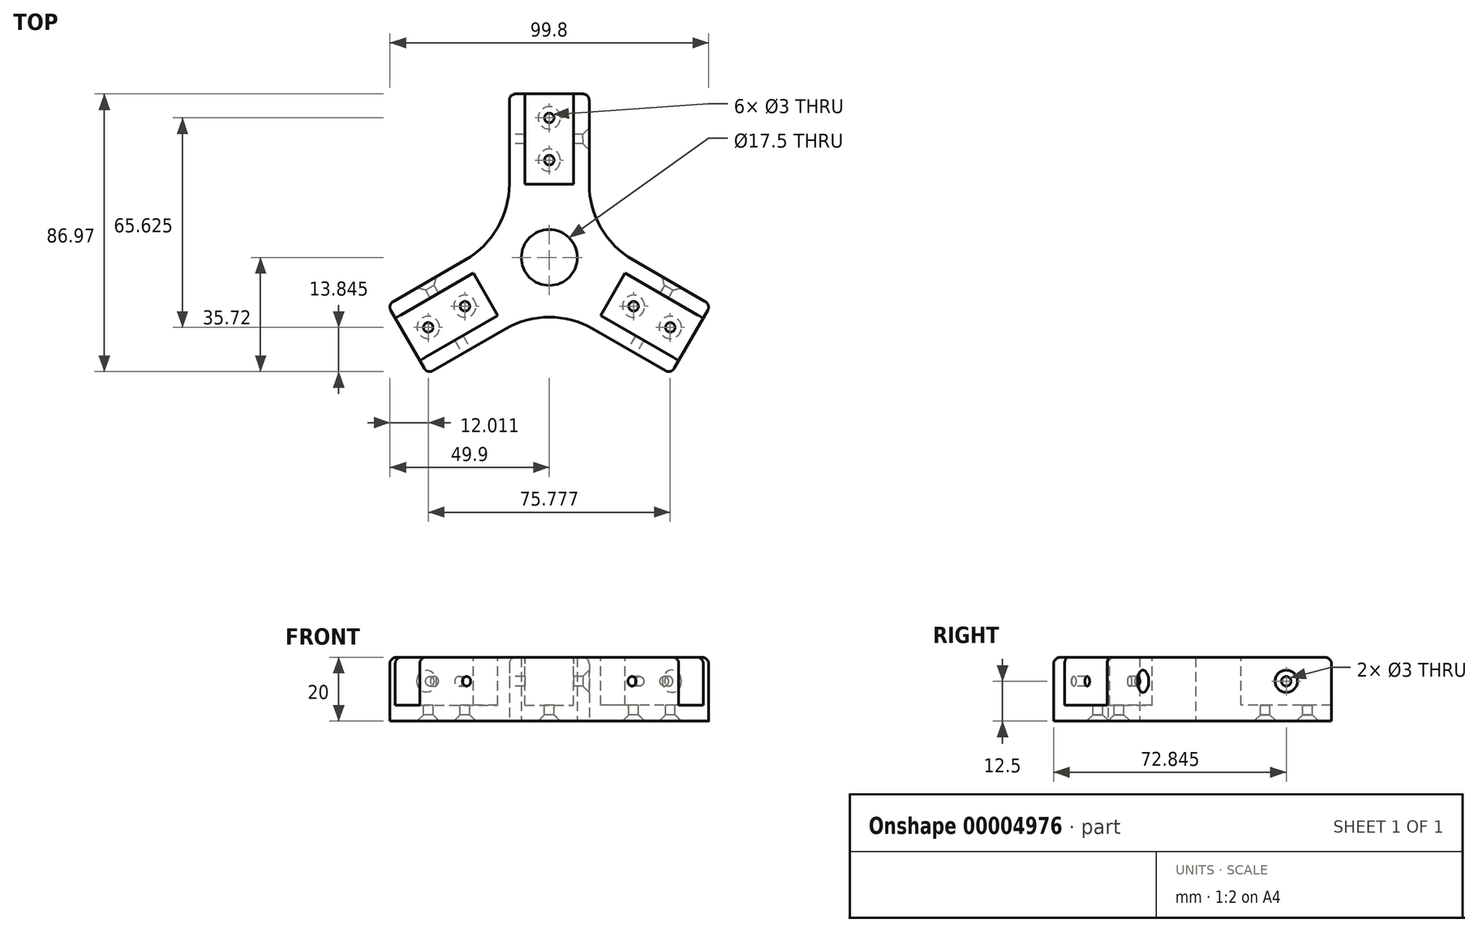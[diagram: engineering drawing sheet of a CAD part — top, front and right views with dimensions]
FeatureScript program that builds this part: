
annotation { "Feature Type Name" : "Feature", "Feature Type Description" : "" }
export const myFeature = defineFeature(function(context is Context, id is Id, definition is map)
    precondition{}
    {
        {
            var Q0;
            Q0=qCreatedBy(makeId("Top.planeOp"),FACE);
            var sketch = newSketch(context, id + "F0", { "sketchPlane" : qUnion([Q0])});
            skCircle(sketch, "E0", {"center": v(0, 0) * mm, "radius": 6.25 * mm, "construction": true});
            skLineSegment(sketch, "E1", {"start": v(0, 0) * mm, "end": v(0, 51.25) * mm, "construction": true});
            skLineSegment(sketch, "E2", {"start": v(-12.5, 51.25) * mm, "end": v(12.5, 51.25) * mm});
            skLineSegment(sketch, "E3", {"start": v(0, 0) * mm, "end": v(44.38, -25.62) * mm, "construction": true});
            skLineSegment(sketch, "E4", {"start": v(12.5, 51.25) * mm, "end": v(12.5, 23) * mm});
            skLineSegment(sketch, "E5", {"start": v(38.13, -36.45) * mm, "end": v(50.63, -14.8) * mm});
            skLineSegment(sketch, "E6", {"start": v(50.63, -14.8) * mm, "end": v(26.17, -0.67) * mm});
            skArc(sketch, "E7", {"start": v(12.5, 23) * mm, "mid": v(16.16, 9.33) * mm, "end": v(26.17, -0.67) * mm});
            skPoint(sketch, "E8", {"position": v(0, 6.25) * mm});
            skLineSegment(sketch, "E9.1.0", {"start": v(-50.63, -14.8) * mm, "end": v(-26.17, -0.67) * mm});
            skArc(sketch, "E9.1.1", {"start": v(-26.17, -0.67) * mm, "mid": v(-16.16, 9.33) * mm, "end": v(-12.5, 23) * mm});
            skLineSegment(sketch, "E9.1.2", {"start": v(-12.5, 51.25) * mm, "end": v(-12.5, 23) * mm});
            skLineSegment(sketch, "E9.2.0", {"start": v(38.13, -36.45) * mm, "end": v(13.67, -22.33) * mm});
            skArc(sketch, "E9.2.1", {"start": v(13.67, -22.33) * mm, "mid": v(0, -18.66) * mm, "end": v(-13.67, -22.33) * mm});
            skLineSegment(sketch, "E9.2.2", {"start": v(-38.13, -36.45) * mm, "end": v(-13.67, -22.33) * mm});
            skLineSegment(sketch, "E10", {"start": v(-50.63, -14.8) * mm, "end": v(-38.13, -36.45) * mm});
            skLineSegment(sketch, "E11", {"start": v(-12.5, 23) * mm, "end": v(12.5, 23) * mm, "construction": true});
            skCircle(sketch, "E12", {"center": v(0, 0) * mm, "radius": 8.75 * mm});
            skSolve(sketch);
        }
        {
            var Q0;
            Q0 = qSketchRegion(id + "F0", true);
            extrude(context, id + "F1", {"entities" : qUnion([Q0]), "depth" : 20 * mm});
        }
        {
            var Q0;
            Q0=makeQuery(id+"F1.opExtrude","CAP_FACE",FACE,{"disambiguationData":[OSD([sQuery(id+"F0.wireOp",EDGE,"E0"),sQuery(id+"F0.wireOp",EDGE,"E2"),sQuery(id+"F0.wireOp",EDGE,"E4"),sQuery(id+"F0.wireOp",EDGE,"E5"),sQuery(id+"F0.wireOp",EDGE,"E6"),sQuery(id+"F0.wireOp",EDGE,"E7"),sQuery(id+"F0.wireOp",EDGE,"E9.1.0"),sQuery(id+"F0.wireOp",EDGE,"E9.1.1"),sQuery(id+"F0.wireOp",EDGE,"E9.1.2"),sQuery(id+"F0.wireOp",EDGE,"E9.2.0"),sQuery(id+"F0.wireOp",EDGE,"E9.2.1"),sQuery(id+"F0.wireOp",EDGE,"E9.2.2"),sQuery(id+"F0.wireOp",EDGE,"E10")])],"isStart":false});
            var sketch = newSketch(context, id + "F2", { "sketchPlane" : qUnion([Q0])});
            skLineSegment(sketch, "E13", {"start": v(0, 0) * mm, "end": v(0, 51.25) * mm, "construction": true});
            skLineSegment(sketch, "E14", {"start": v(-12.5, 23) * mm, "end": v(12.5, 23) * mm, "construction": true});
            skLineSegment(sketch, "E15.bottom", {"start": v(-7.68, 51.25) * mm, "end": v(7.67, 51.25) * mm});
            skLineSegment(sketch, "E15.top", {"start": v(-7.68, 23) * mm, "end": v(7.67, 23) * mm});
            skLineSegment(sketch, "E15.left", {"start": v(-7.68, 51.25) * mm, "end": v(-7.68, 23) * mm});
            skLineSegment(sketch, "E15.right", {"start": v(7.67, 51.25) * mm, "end": v(7.67, 23) * mm});
            skLineSegment(sketch, "E16.1.0", {"start": v(-48.22, -18.98) * mm, "end": v(-23.76, -4.85) * mm});
            skLineSegment(sketch, "E16.1.1", {"start": v(-40.55, -32.27) * mm, "end": v(-48.22, -18.98) * mm});
            skLineSegment(sketch, "E16.1.2", {"start": v(-40.55, -32.27) * mm, "end": v(-16.08, -18.15) * mm});
            skLineSegment(sketch, "E16.1.3", {"start": v(-16.08, -18.15) * mm, "end": v(-23.76, -4.85) * mm});
            skLineSegment(sketch, "E16.2.0", {"start": v(40.55, -32.27) * mm, "end": v(16.08, -18.15) * mm});
            skLineSegment(sketch, "E16.2.1", {"start": v(48.22, -18.98) * mm, "end": v(40.55, -32.27) * mm});
            skLineSegment(sketch, "E16.2.2", {"start": v(48.22, -18.98) * mm, "end": v(23.76, -4.85) * mm});
            skLineSegment(sketch, "E16.2.3", {"start": v(23.76, -4.85) * mm, "end": v(16.08, -18.15) * mm});
            skPoint(sketch, "E16.center", {"position": v(0, 0) * mm});
            skSolve(sketch);
        }
        {
            var Q0;
            Q0 = qSketchRegion(id + "F2", true);
            extrude(context, id + "F3", {"entities" : qUnion([Q0]), "operationType" : NewBodyOperationType.REMOVE, "oppositeDirection" : true, "depth" : 15 * mm});
        }
        {
            var Q0;
            Q0=makeQuery(id+"F3.boolean.opBoolean","COPY",FACE,{"derivedFrom":makeQuery(id+"F3.opExtrude","CAP_FACE",FACE,{"disambiguationData":[OSD([sQuery(id+"F2.wireOp",EDGE,"E15.bottom"),sQuery(id+"F2.wireOp",EDGE,"E15.top"),sQuery(id+"F2.wireOp",EDGE,"E15.left"),sQuery(id+"F2.wireOp",EDGE,"E15.right")])],"isStart":false})});
            var sketch = newSketch(context, id + "F4", { "sketchPlane" : qUnion([Q0])});
            skLineSegment(sketch, "E17", {"start": v(0, 51.25) * mm, "end": v(0, 23) * mm, "construction": true});
            skCircle(sketch, "E18", {"center": v(0, 43.75) * mm, "radius": 1.5 * mm});
            skCircle(sketch, "E19", {"center": v(0, 30.5) * mm, "radius": 1.5 * mm});
            skCircle(sketch, "E20.1.0", {"center": v(-37.89, -21.87) * mm, "radius": 1.5 * mm});
            skCircle(sketch, "E20.1.1", {"center": v(-26.41, -15.25) * mm, "radius": 1.5 * mm});
            skCircle(sketch, "E20.2.0", {"center": v(37.89, -21.87) * mm, "radius": 1.5 * mm});
            skCircle(sketch, "E20.2.1", {"center": v(26.41, -15.25) * mm, "radius": 1.5 * mm});
            skPoint(sketch, "E20.center", {"position": v(0, 0) * mm});
            skSolve(sketch);
        }
        {
            var Q0;
            Q0 = qSketchRegion(id + "F4", true);
            extrude(context, id + "F5", {"entities" : qUnion([Q0]), "operationType" : NewBodyOperationType.REMOVE, "endBound" : BoundingType.THROUGH_ALL, "oppositeDirection" : true, "depth" : 25 * mm});
        }
        {
            var Q0;
            {var subQ0=sQuery(id+"F0.wireOp",EDGE,"E2");var subQ1=sQuery(id+"F0.wireOp",EDGE,"E9.1.2");Q0=makeQuery(id+"F3.boolean.opBoolean","SPLIT",EDGE,{"disambiguationData":[TD([makeQuery(id+"F1.opExtrude","SWEPT_FACE",FACE,{"disambiguationData":[OSD([subQ1])]})])],"derivedFrom":makeQuery(id+"F1.opExtrude","CAP_EDGE",EDGE,{"disambiguationData":[OSD([subQ0])],"isStart":false})});}
            var Q1;
            {var subQ0=sQuery(id+"F0.wireOp",EDGE,"E2");var subQ1=sQuery(id+"F0.wireOp",EDGE,"E4");Q1=makeQuery(id+"F3.boolean.opBoolean","SPLIT",EDGE,{"disambiguationData":[TD([makeQuery(id+"F1.opExtrude","SWEPT_FACE",FACE,{"disambiguationData":[OSD([subQ1])]})])],"derivedFrom":makeQuery(id+"F1.opExtrude","CAP_EDGE",EDGE,{"disambiguationData":[OSD([subQ0])],"isStart":false})});}
            var Q2;
            {var subQ0=sQuery(id+"F0.wireOp",EDGE,"E5");var subQ1=sQuery(id+"F0.wireOp",EDGE,"E6");Q2=makeQuery(id+"F3.boolean.opBoolean","SPLIT",EDGE,{"disambiguationData":[TD([makeQuery(id+"F1.opExtrude","SWEPT_FACE",FACE,{"disambiguationData":[OSD([subQ1])]})])],"derivedFrom":makeQuery(id+"F1.opExtrude","CAP_EDGE",EDGE,{"disambiguationData":[OSD([subQ0])],"isStart":false})});}
            var Q3;
            {var subQ0=sQuery(id+"F0.wireOp",EDGE,"E5");var subQ1=sQuery(id+"F0.wireOp",EDGE,"E9.2.0");Q3=makeQuery(id+"F3.boolean.opBoolean","SPLIT",EDGE,{"disambiguationData":[TD([makeQuery(id+"F1.opExtrude","SWEPT_FACE",FACE,{"disambiguationData":[OSD([subQ1])]})])],"derivedFrom":makeQuery(id+"F1.opExtrude","CAP_EDGE",EDGE,{"disambiguationData":[OSD([subQ0])],"isStart":false})});}
            var Q4;
            {var subQ0=sQuery(id+"F0.wireOp",EDGE,"E10");var subQ1=sQuery(id+"F0.wireOp",EDGE,"E9.2.2");Q4=makeQuery(id+"F3.boolean.opBoolean","SPLIT",EDGE,{"disambiguationData":[TD([makeQuery(id+"F1.opExtrude","SWEPT_FACE",FACE,{"disambiguationData":[OSD([subQ1])]})])],"derivedFrom":makeQuery(id+"F1.opExtrude","CAP_EDGE",EDGE,{"disambiguationData":[OSD([subQ0])],"isStart":false})});}
            var Q5;
            {var subQ0=sQuery(id+"F0.wireOp",EDGE,"E10");var subQ1=sQuery(id+"F0.wireOp",EDGE,"E9.1.0");Q5=makeQuery(id+"F3.boolean.opBoolean","SPLIT",EDGE,{"disambiguationData":[TD([makeQuery(id+"F1.opExtrude","SWEPT_FACE",FACE,{"disambiguationData":[OSD([subQ1])]})])],"derivedFrom":makeQuery(id+"F1.opExtrude","CAP_EDGE",EDGE,{"disambiguationData":[OSD([subQ0])],"isStart":false})});}
            fillet(context, id + "F6", {"entities" : qUnion([Q0, Q1, Q2, Q3, Q4, Q5]), "radius" : 2 * mm, "tangentPropagation" : true, "allowEdgeOverflow" : false});
        }
        {
            var Q0;
            Q0=makeQuery(id+"F1.opExtrude","SWEPT_FACE",FACE,{"disambiguationData":[OSD([sQuery(id+"F0.wireOp",EDGE,"E9.2.2")])]});
            var sketch = newSketch(context, id + "F7", { "sketchPlane" : qUnion([Q0])});
            skLineSegment(sketch, "E21.0", {"start": v(-23, 5) * mm, "end": v(-23, 20) * mm, "construction": true});
            skLineSegment(sketch, "E22", {"start": v(-23, 12.5) * mm, "end": v(-51.25, 12.5) * mm, "construction": true});
            skCircle(sketch, "E23", {"center": v(-37.12, 12.5) * mm, "radius": 1.5 * mm});
            skSolve(sketch);
        }
        {
            var Q0;
            Q0 = qSketchRegion(id + "F7", true);
            extrude(context, id + "F8", {"entities" : qUnion([Q0]), "operationType" : NewBodyOperationType.REMOVE, "endBound" : BoundingType.THROUGH_ALL, "oppositeDirection" : true, "depth" : 25 * mm});
        }
        {
            var Q0;
            Q0=makeQuery(id+"F1.opExtrude","SWEPT_FACE",FACE,{"disambiguationData":[OSD([sQuery(id+"F0.wireOp",EDGE,"E9.2.0")])]});
            var sketch = newSketch(context, id + "F9", { "sketchPlane" : qUnion([Q0])});
            skLineSegment(sketch, "E24.0", {"start": v(23, 5) * mm, "end": v(23, 20) * mm, "construction": true});
            skLineSegment(sketch, "E25", {"start": v(23, 12.5) * mm, "end": v(51.25, 12.5) * mm, "construction": true});
            skCircle(sketch, "E26", {"center": v(37.12, 12.5) * mm, "radius": 1.5 * mm});
            skSolve(sketch);
        }
        {
            var Q0;
            Q0 = qSketchRegion(id + "F9", true);
            extrude(context, id + "F10", {"entities" : qUnion([Q0]), "operationType" : NewBodyOperationType.REMOVE, "endBound" : BoundingType.THROUGH_ALL, "oppositeDirection" : true, "depth" : 25 * mm});
        }
        {
            var Q0;
            Q0=makeQuery(id+"F1.opExtrude","SWEPT_FACE",FACE,{"disambiguationData":[OSD([sQuery(id+"F0.wireOp",EDGE,"E9.1.2")])]});
            var sketch = newSketch(context, id + "F11", { "sketchPlane" : qUnion([Q0])});
            skLineSegment(sketch, "E27.0", {"start": v(-23, 5) * mm, "end": v(-23, 20) * mm, "construction": true});
            skLineSegment(sketch, "E28", {"start": v(-23, 12.5) * mm, "end": v(-51.25, 12.5) * mm, "construction": true});
            skCircle(sketch, "E29", {"center": v(-37.13, 12.5) * mm, "radius": 1.5 * mm});
            skSolve(sketch);
        }
        {
            var Q0;
            Q0 = qSketchRegion(id + "F11", true);
            extrude(context, id + "F12", {"entities" : qUnion([Q0]), "operationType" : NewBodyOperationType.REMOVE, "endBound" : BoundingType.THROUGH_ALL, "oppositeDirection" : true, "depth" : 25 * mm});
        }
        {
            var Q0;
            Q0=makeQuery(id+"F1.opExtrude","SWEPT_EDGE",EDGE,{"disambiguationData":[OSD([sQuery(id+"F0.wireOp",EDGE,"E5"),sQuery(id+"F0.wireOp",EDGE,"E9.2.0")])]});
            var Q1;
            Q1=makeQuery(id+"F1.opExtrude","SWEPT_EDGE",EDGE,{"disambiguationData":[OSD([sQuery(id+"F0.wireOp",EDGE,"E5"),sQuery(id+"F0.wireOp",EDGE,"E6")])]});
            var Q2;
            Q2=makeQuery(id+"F1.opExtrude","SWEPT_EDGE",EDGE,{"disambiguationData":[OSD([sQuery(id+"F0.wireOp",EDGE,"E9.1.0"),sQuery(id+"F0.wireOp",EDGE,"E10")])]});
            fillet(context, id + "F13", {"entities" : qUnion([Q0, Q1, Q2]), "radius" : 2 * mm, "tangentPropagation" : true, "defaultsChanged" : true, "vertexSettings" : [], "allowEdgeOverflow" : false});
        }
        {
            var Q0;
            Q0=makeQuery(id+"F8.boolean.opBoolean","COPY",EDGE,{"derivedFrom":makeQuery(id+"F8.opExtrude","CAP_EDGE",EDGE,{"disambiguationData":[OSD([sQuery(id+"F7.wireOp",EDGE,"E23")])],"isStart":true})});
            var Q1;
            Q1=makeQuery(id+"F10.boolean.opBoolean","COPY",EDGE,{"derivedFrom":makeQuery(id+"F10.opExtrude","CAP_EDGE",EDGE,{"disambiguationData":[OSD([sQuery(id+"F9.wireOp",EDGE,"E26")])],"isStart":true})});
            var Q2;
            Q2=makeQuery(id+"F10.boolean.opBoolean","INTERSECT",EDGE,{"derivedFrom":[makeQuery(id+"F1.opExtrude","SWEPT_FACE",FACE,{"disambiguationData":[OSD([sQuery(id+"F0.wireOp",EDGE,"E6")])]}),makeQuery(id+"F10.opExtrude","SWEPT_FACE",FACE,{"disambiguationData":[OSD([sQuery(id+"F9.wireOp",EDGE,"E26")])]})]});
            var Q3;
            Q3=makeQuery(id+"F12.boolean.opBoolean","INTERSECT",EDGE,{"derivedFrom":[makeQuery(id+"F1.opExtrude","SWEPT_FACE",FACE,{"disambiguationData":[OSD([sQuery(id+"F0.wireOp",EDGE,"E4")])]}),makeQuery(id+"F12.opExtrude","SWEPT_FACE",FACE,{"disambiguationData":[OSD([sQuery(id+"F11.wireOp",EDGE,"E29")])]})]});
            var Q4;
            Q4=makeQuery(id+"F12.boolean.opBoolean","COPY",EDGE,{"derivedFrom":makeQuery(id+"F12.opExtrude","CAP_EDGE",EDGE,{"disambiguationData":[OSD([sQuery(id+"F11.wireOp",EDGE,"E29")])],"isStart":true})});
            var Q5;
            Q5=makeQuery(id+"F8.boolean.opBoolean","INTERSECT",EDGE,{"derivedFrom":[makeQuery(id+"F1.opExtrude","SWEPT_FACE",FACE,{"disambiguationData":[OSD([sQuery(id+"F0.wireOp",EDGE,"E9.1.0")])]}),makeQuery(id+"F8.opExtrude","SWEPT_FACE",FACE,{"disambiguationData":[OSD([sQuery(id+"F7.wireOp",EDGE,"E23")])]})]});
            var Q6;
            Q6=makeQuery(id+"F5.boolean.opBoolean","INTERSECT",EDGE,{"derivedFrom":[makeQuery(id+"F1.opExtrude","CAP_FACE",FACE,{"disambiguationData":[OSD([sQuery(id+"F0.wireOp",EDGE,"E2"),sQuery(id+"F0.wireOp",EDGE,"E4"),sQuery(id+"F0.wireOp",EDGE,"E5"),sQuery(id+"F0.wireOp",EDGE,"E6"),sQuery(id+"F0.wireOp",EDGE,"E7"),sQuery(id+"F0.wireOp",EDGE,"E9.1.0"),sQuery(id+"F0.wireOp",EDGE,"E9.1.1"),sQuery(id+"F0.wireOp",EDGE,"E9.1.2"),sQuery(id+"F0.wireOp",EDGE,"E9.2.0"),sQuery(id+"F0.wireOp",EDGE,"E9.2.1"),sQuery(id+"F0.wireOp",EDGE,"E9.2.2"),sQuery(id+"F0.wireOp",EDGE,"E10"),sQuery(id+"F0.wireOp",EDGE,"E12")])],"isStart":true}),makeQuery(id+"F5.opExtrude","SWEPT_FACE",FACE,{"disambiguationData":[OSD([sQuery(id+"F4.wireOp",EDGE,"E18")])]})]});
            var Q7;
            Q7=makeQuery(id+"F5.boolean.opBoolean","INTERSECT",EDGE,{"derivedFrom":[makeQuery(id+"F1.opExtrude","CAP_FACE",FACE,{"disambiguationData":[OSD([sQuery(id+"F0.wireOp",EDGE,"E2"),sQuery(id+"F0.wireOp",EDGE,"E4"),sQuery(id+"F0.wireOp",EDGE,"E5"),sQuery(id+"F0.wireOp",EDGE,"E6"),sQuery(id+"F0.wireOp",EDGE,"E7"),sQuery(id+"F0.wireOp",EDGE,"E9.1.0"),sQuery(id+"F0.wireOp",EDGE,"E9.1.1"),sQuery(id+"F0.wireOp",EDGE,"E9.1.2"),sQuery(id+"F0.wireOp",EDGE,"E9.2.0"),sQuery(id+"F0.wireOp",EDGE,"E9.2.1"),sQuery(id+"F0.wireOp",EDGE,"E9.2.2"),sQuery(id+"F0.wireOp",EDGE,"E10"),sQuery(id+"F0.wireOp",EDGE,"E12")])],"isStart":true}),makeQuery(id+"F5.opExtrude","SWEPT_FACE",FACE,{"disambiguationData":[OSD([sQuery(id+"F4.wireOp",EDGE,"E19")])]})]});
            var Q8;
            Q8=makeQuery(id+"F5.boolean.opBoolean","INTERSECT",EDGE,{"derivedFrom":[makeQuery(id+"F1.opExtrude","CAP_FACE",FACE,{"disambiguationData":[OSD([sQuery(id+"F0.wireOp",EDGE,"E2"),sQuery(id+"F0.wireOp",EDGE,"E4"),sQuery(id+"F0.wireOp",EDGE,"E5"),sQuery(id+"F0.wireOp",EDGE,"E6"),sQuery(id+"F0.wireOp",EDGE,"E7"),sQuery(id+"F0.wireOp",EDGE,"E9.1.0"),sQuery(id+"F0.wireOp",EDGE,"E9.1.1"),sQuery(id+"F0.wireOp",EDGE,"E9.1.2"),sQuery(id+"F0.wireOp",EDGE,"E9.2.0"),sQuery(id+"F0.wireOp",EDGE,"E9.2.1"),sQuery(id+"F0.wireOp",EDGE,"E9.2.2"),sQuery(id+"F0.wireOp",EDGE,"E10"),sQuery(id+"F0.wireOp",EDGE,"E12")])],"isStart":true}),makeQuery(id+"F5.opExtrude","SWEPT_FACE",FACE,{"disambiguationData":[OSD([sQuery(id+"F4.wireOp",EDGE,"E20.1.1")])]})]});
            var Q9;
            Q9=makeQuery(id+"F5.boolean.opBoolean","INTERSECT",EDGE,{"derivedFrom":[makeQuery(id+"F1.opExtrude","CAP_FACE",FACE,{"disambiguationData":[OSD([sQuery(id+"F0.wireOp",EDGE,"E2"),sQuery(id+"F0.wireOp",EDGE,"E4"),sQuery(id+"F0.wireOp",EDGE,"E5"),sQuery(id+"F0.wireOp",EDGE,"E6"),sQuery(id+"F0.wireOp",EDGE,"E7"),sQuery(id+"F0.wireOp",EDGE,"E9.1.0"),sQuery(id+"F0.wireOp",EDGE,"E9.1.1"),sQuery(id+"F0.wireOp",EDGE,"E9.1.2"),sQuery(id+"F0.wireOp",EDGE,"E9.2.0"),sQuery(id+"F0.wireOp",EDGE,"E9.2.1"),sQuery(id+"F0.wireOp",EDGE,"E9.2.2"),sQuery(id+"F0.wireOp",EDGE,"E10"),sQuery(id+"F0.wireOp",EDGE,"E12")])],"isStart":true}),makeQuery(id+"F5.opExtrude","SWEPT_FACE",FACE,{"disambiguationData":[OSD([sQuery(id+"F4.wireOp",EDGE,"E20.1.0")])]})]});
            var Q10;
            Q10=makeQuery(id+"F5.boolean.opBoolean","INTERSECT",EDGE,{"derivedFrom":[makeQuery(id+"F1.opExtrude","CAP_FACE",FACE,{"disambiguationData":[OSD([sQuery(id+"F0.wireOp",EDGE,"E2"),sQuery(id+"F0.wireOp",EDGE,"E4"),sQuery(id+"F0.wireOp",EDGE,"E5"),sQuery(id+"F0.wireOp",EDGE,"E6"),sQuery(id+"F0.wireOp",EDGE,"E7"),sQuery(id+"F0.wireOp",EDGE,"E9.1.0"),sQuery(id+"F0.wireOp",EDGE,"E9.1.1"),sQuery(id+"F0.wireOp",EDGE,"E9.1.2"),sQuery(id+"F0.wireOp",EDGE,"E9.2.0"),sQuery(id+"F0.wireOp",EDGE,"E9.2.1"),sQuery(id+"F0.wireOp",EDGE,"E9.2.2"),sQuery(id+"F0.wireOp",EDGE,"E10"),sQuery(id+"F0.wireOp",EDGE,"E12")])],"isStart":true}),makeQuery(id+"F5.opExtrude","SWEPT_FACE",FACE,{"disambiguationData":[OSD([sQuery(id+"F4.wireOp",EDGE,"E20.2.1")])]})]});
            var Q11;
            Q11=makeQuery(id+"F5.boolean.opBoolean","INTERSECT",EDGE,{"derivedFrom":[makeQuery(id+"F1.opExtrude","CAP_FACE",FACE,{"disambiguationData":[OSD([sQuery(id+"F0.wireOp",EDGE,"E2"),sQuery(id+"F0.wireOp",EDGE,"E4"),sQuery(id+"F0.wireOp",EDGE,"E5"),sQuery(id+"F0.wireOp",EDGE,"E6"),sQuery(id+"F0.wireOp",EDGE,"E7"),sQuery(id+"F0.wireOp",EDGE,"E9.1.0"),sQuery(id+"F0.wireOp",EDGE,"E9.1.1"),sQuery(id+"F0.wireOp",EDGE,"E9.1.2"),sQuery(id+"F0.wireOp",EDGE,"E9.2.0"),sQuery(id+"F0.wireOp",EDGE,"E9.2.1"),sQuery(id+"F0.wireOp",EDGE,"E9.2.2"),sQuery(id+"F0.wireOp",EDGE,"E10"),sQuery(id+"F0.wireOp",EDGE,"E12")])],"isStart":true}),makeQuery(id+"F5.opExtrude","SWEPT_FACE",FACE,{"disambiguationData":[OSD([sQuery(id+"F4.wireOp",EDGE,"E20.2.0")])]})]});
            chamfer(context, id + "F14", {"entities" : qUnion([Q0, Q1, Q2, Q3, Q4, Q5, Q6, Q7, Q8, Q9, Q10, Q11]), "width" : 2 * mm, "tangentPropagation" : true});
        }
    });
